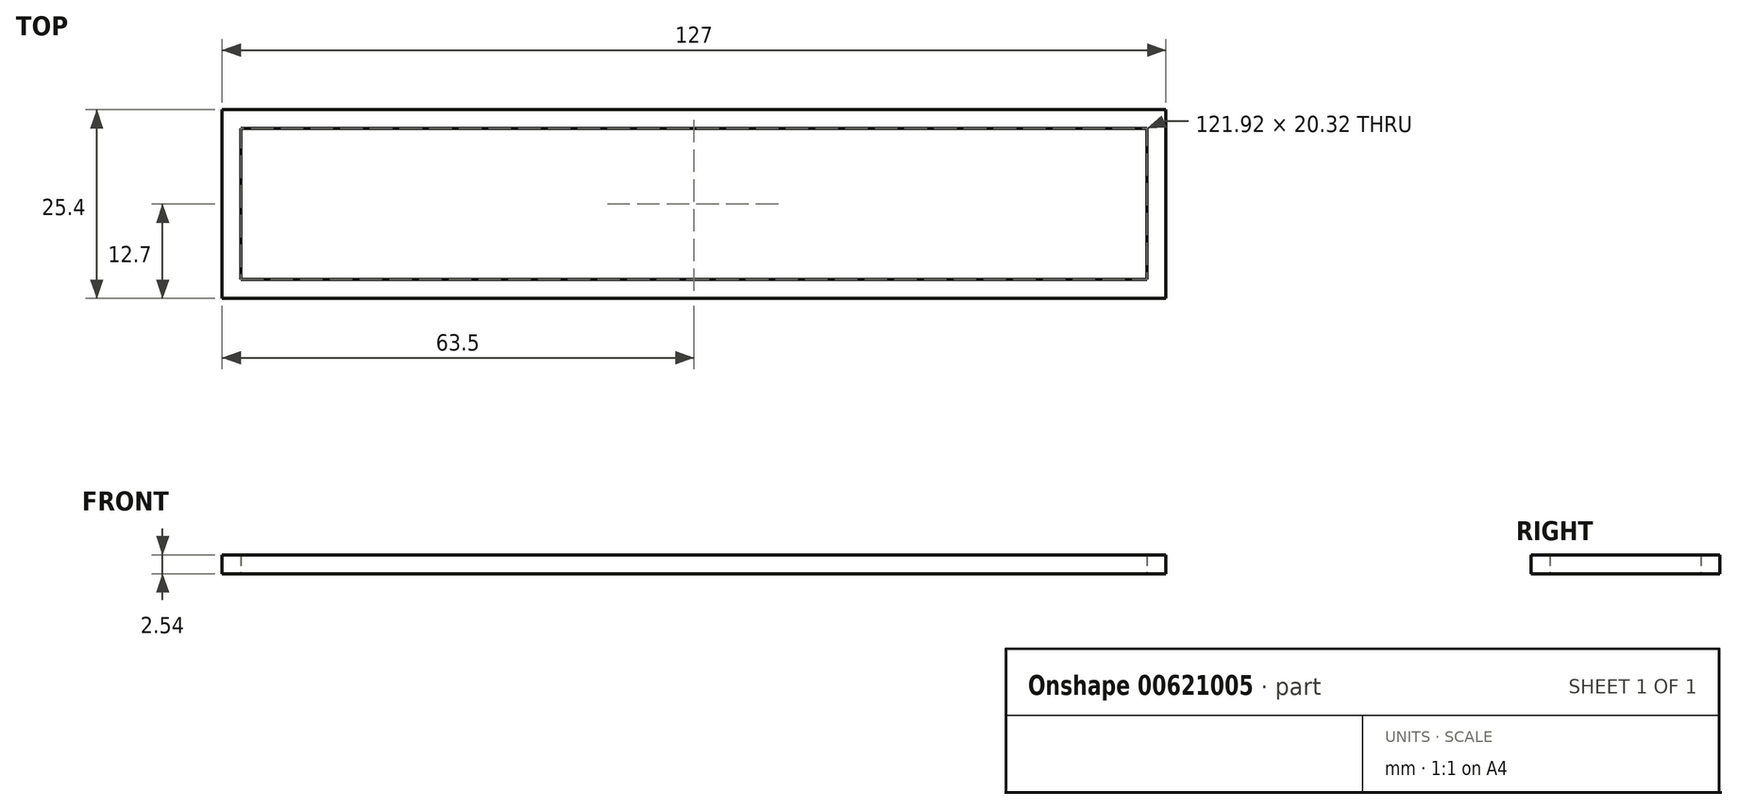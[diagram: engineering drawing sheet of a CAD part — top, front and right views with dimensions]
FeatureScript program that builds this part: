
annotation { "Feature Type Name" : "Feature", "Feature Type Description" : "" }
export const myFeature = defineFeature(function(context is Context, id is Id, definition is map)
    precondition{}
    {
        {
            var Q0;
            Q0=qCreatedBy(makeId("Top.planeOp"),FACE);
            var sketch = newSketch(context, id + "F0", { "sketchPlane" : qUnion([Q0])});
            skLineSegment(sketch, "E0", {"start": v(0, 0) * mm, "end": v(127, 0) * mm});
            skLineSegment(sketch, "E1", {"start": v(0, 0) * mm, "end": v(0, 25.4) * mm});
            skLineSegment(sketch, "E2", {"start": v(0, 25.4) * mm, "end": v(127, 25.4) * mm});
            skLineSegment(sketch, "E3", {"start": v(127, 25.4) * mm, "end": v(127, 0) * mm});
            skLineSegment(sketch, "E4.0", {"start": v(2.54, 2.54) * mm, "end": v(2.54, 22.86) * mm});
            skLineSegment(sketch, "E4.1", {"start": v(2.54, 2.54) * mm, "end": v(124.46, 2.54) * mm});
            skLineSegment(sketch, "E4.2", {"start": v(124.46, 22.86) * mm, "end": v(124.46, 2.54) * mm});
            skLineSegment(sketch, "E4.3", {"start": v(2.54, 22.86) * mm, "end": v(124.46, 22.86) * mm});
            skSolve(sketch);
        }
        {
            var Q0;
            Q0 = qSketchRegion(id + "F0", true);
            extrude(context, id + "F1", {"entities" : qUnion([Q0]), "depth" : 2.54 * mm, "offsetDistance" : 25.4 * mm});
        }
    });
